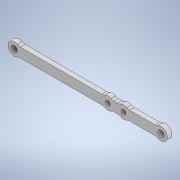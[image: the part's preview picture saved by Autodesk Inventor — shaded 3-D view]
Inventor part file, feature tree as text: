
AUTODESK INVENTOR PART (.ipt)
format: ipt  version: 2020 (Build 240168000, 168)  size: 162,304 bytes
history: native  units: mm
features: extrude x3, sketch x3, fillet x2
ambient origin geometry x8: Origin, YZ Plane, XZ Plane, XY Plane, X Axis, Y Axis, Z Axis, Center Point
bodies: Solid1 (feature_tree)
feature tree (8):
  extrude  "Extrusion1"  Depth=4.0mm
  fillet  "Fillet2"  Radius=1.5mm
  extrude  "Extrusion2"  Depth=47.0mm
  extrude  "Extrusion3"  Depth=2.0mm
  fillet  "Fillet3"  Radius=5.0mm
  sketch  "Sketch1"  dims[d0=2.0mm d1=4.0mm d4=1.5mm d5=0.0mm]
  sketch  "Sketch3"  dims[d8=3.0mm d9=47.0mm]
  sketch  "Sketch4"  dims[d10=2.0mm d11=12.0mm d12=5.0mm d13=1.5mm d14=0.0mm d15=0.0mm d16=4.0mm d17=1.5mm d18=0.0mm d19=2.0mm]
